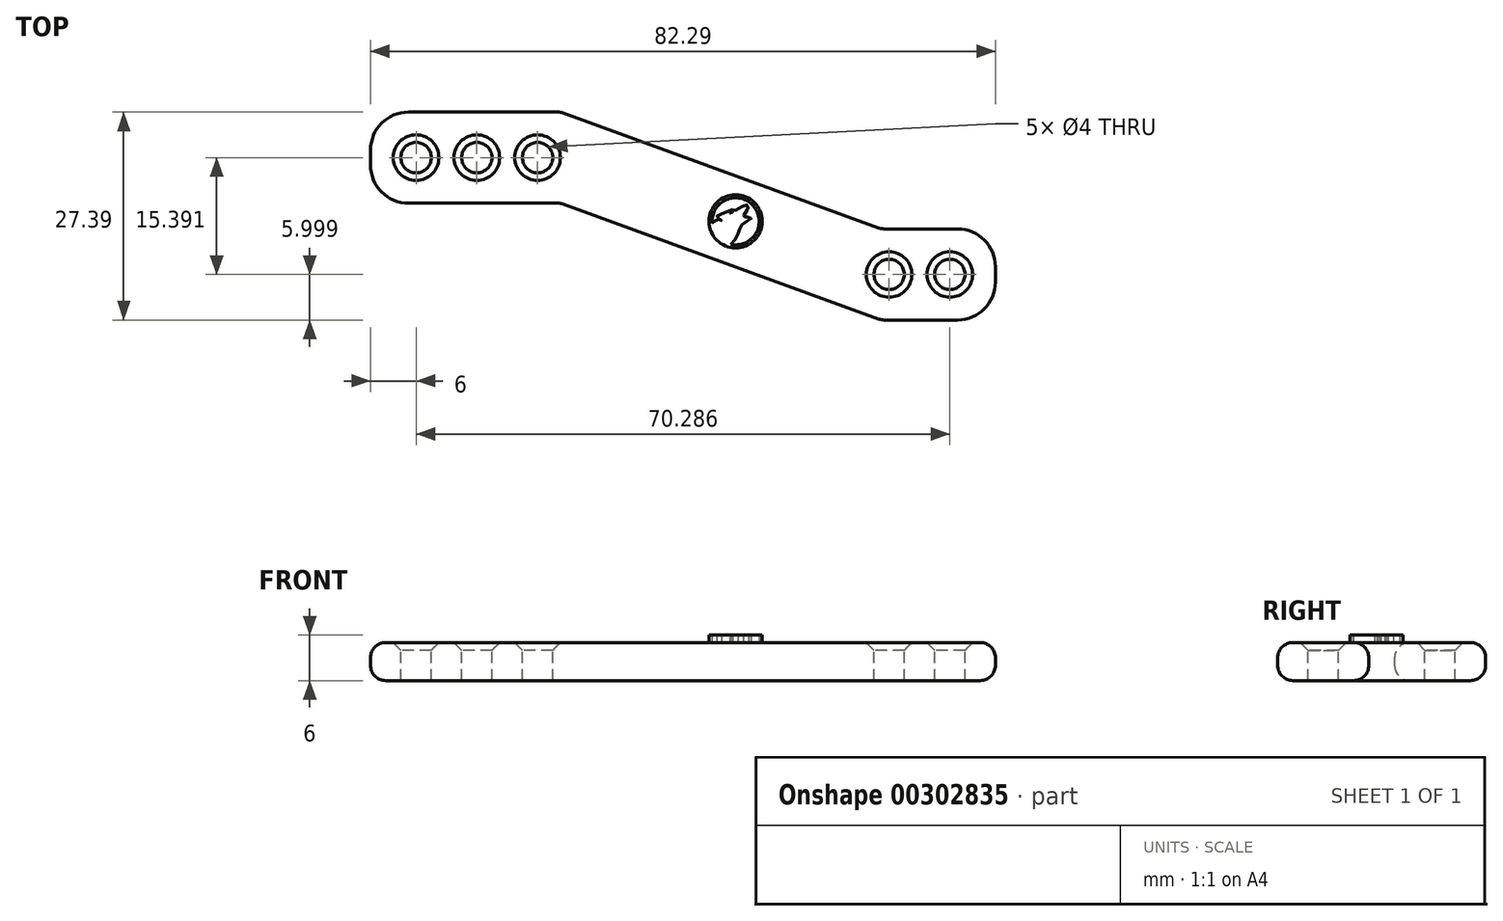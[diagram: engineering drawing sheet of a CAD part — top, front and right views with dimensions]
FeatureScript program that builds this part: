
annotation { "Feature Type Name" : "Feature", "Feature Type Description" : "" }
export const myFeature = defineFeature(function(context is Context, id is Id, definition is map)
    precondition{}
    {
        {
            var Q0;
            Q0=qCreatedBy(makeId("Top.planeOp"),FACE);
            var sketch = newSketch(context, id + "F0", { "sketchPlane" : qUnion([Q0])});
            skLineSegment(sketch, "E0.bottom", {"start": v(0, 0) * mm, "end": v(25, 0) * mm});
            skLineSegment(sketch, "E0.top", {"start": v(0, 12) * mm, "end": v(25, 12) * mm});
            skLineSegment(sketch, "E0.left", {"start": v(0, 0) * mm, "end": v(0, 12) * mm});
            skLineSegment(sketch, "E0.right", {"start": v(25, 0) * mm, "end": v(25, 12) * mm});
            skLineSegment(sketch, "E1", {"start": v(25, 12) * mm, "end": v(67.29, -3.4) * mm});
            skLineSegment(sketch, "E2.bottom", {"start": v(67.29, -3.4) * mm, "end": v(82.29, -3.4) * mm});
            skLineSegment(sketch, "E2.top", {"start": v(67.29, -15.4) * mm, "end": v(82.29, -15.4) * mm});
            skLineSegment(sketch, "E2.left", {"start": v(67.29, -3.4) * mm, "end": v(67.29, -15.4) * mm});
            skLineSegment(sketch, "E2.right", {"start": v(82.29, -3.4) * mm, "end": v(82.29, -15.4) * mm});
            skLineSegment(sketch, "E3", {"start": v(67.29, -15.4) * mm, "end": v(25, 0) * mm});
            skSolve(sketch);
        }
        {
            var Q0;
            Q0=makeQuery(id+"F0.imprint","IMPRINT",FACE,{"disambiguationData":[TD([[makeQuery(id+"F0.imprint","IMPRINT",EDGE,{"derivedFrom":sQuery(id+"F0.wireOp",EDGE,"E0.bottom")}),1.0]])]});
            var Q1;
            Q1=makeQuery(id+"F0.imprint","IMPRINT",FACE,{"disambiguationData":[TD([[makeQuery(id+"F0.imprint","IMPRINT",EDGE,{"derivedFrom":sQuery(id+"F0.wireOp",EDGE,"E2.bottom")}),-1.0]])]});
            var Q2;
            Q2=makeQuery(id+"F0.imprint","IMPRINT",FACE,{"disambiguationData":[TD([[makeQuery(id+"F0.imprint","IMPRINT",EDGE,{"derivedFrom":sQuery(id+"F0.wireOp",EDGE,"E0.right")}),-1.0]])]});
            extrude(context, id + "F1", {"entities" : qUnion([Q0, Q1, Q2]), "depth" : 5 * mm});
        }
        {
            var Q0;
            Q0=makeQuery(id+"F1.opExtrude","CAP_FACE",FACE,{"disambiguationData":[OSD([sQuery(id+"F0.wireOp",EDGE,"E0.bottom"),sQuery(id+"F0.wireOp",EDGE,"E0.top"),sQuery(id+"F0.wireOp",EDGE,"E0.left"),sQuery(id+"F0.wireOp",EDGE,"E1"),sQuery(id+"F0.wireOp",EDGE,"E2.bottom"),sQuery(id+"F0.wireOp",EDGE,"E2.top"),sQuery(id+"F0.wireOp",EDGE,"E2.right"),sQuery(id+"F0.wireOp",EDGE,"E3")])],"isStart":false});
            var sketch = newSketch(context, id + "F2", { "sketchPlane" : qUnion([Q0])});
            skCircle(sketch, "E4", {"center": v(6, 6) * mm, "radius": 2 * mm});
            skPoint(sketch, "E4.centerSnap0", {"position": v(0, 6) * mm});
            skCircle(sketch, "E5", {"center": v(76.29, -9.4) * mm, "radius": 2 * mm});
            skPoint(sketch, "E5.centerSnap0", {"position": v(82.29, -9.4) * mm});
            skCircle(sketch, "E6.1.0.0", {"center": v(14, 6) * mm, "radius": 2 * mm});
            skCircle(sketch, "E6.2.0.0", {"center": v(22, 6) * mm, "radius": 2 * mm});
            skLineSegment(sketch, "E6.direction1", {"start": v(6, 6) * mm, "end": v(14, 6) * mm, "construction": true});
            skCircle(sketch, "E7.1.0.0", {"center": v(68.29, -9.4) * mm, "radius": 2 * mm});
            skLineSegment(sketch, "E7.direction1", {"start": v(76.29, -9.4) * mm, "end": v(68.29, -9.4) * mm, "construction": true});
            skSolve(sketch);
        }
        {
            var Q0;
            Q0=makeQuery(id+"F2.imprint","IMPRINT",FACE,{"disambiguationData":[TD([[makeQuery(id+"F2.imprint","IMPRINT",EDGE,{"derivedFrom":sQuery(id+"F2.wireOp",EDGE,"E4")}),1.0]])]});
            var Q1;
            Q1=makeQuery(id+"F2.imprint","IMPRINT",FACE,{"disambiguationData":[TD([[makeQuery(id+"F2.imprint","IMPRINT",EDGE,{"derivedFrom":sQuery(id+"F2.wireOp",EDGE,"E6.1.0.0")}),1.0]])]});
            var Q2;
            Q2=makeQuery(id+"F2.imprint","IMPRINT",FACE,{"disambiguationData":[TD([[makeQuery(id+"F2.imprint","IMPRINT",EDGE,{"derivedFrom":sQuery(id+"F2.wireOp",EDGE,"E6.2.0.0")}),1.0]])]});
            var Q3;
            Q3=makeQuery(id+"F2.imprint","IMPRINT",FACE,{"disambiguationData":[TD([[makeQuery(id+"F2.imprint","IMPRINT",EDGE,{"derivedFrom":sQuery(id+"F2.wireOp",EDGE,"E7.1.0.0")}),1.0]])]});
            var Q4;
            Q4=makeQuery(id+"F2.imprint","IMPRINT",FACE,{"disambiguationData":[TD([[makeQuery(id+"F2.imprint","IMPRINT",EDGE,{"derivedFrom":sQuery(id+"F2.wireOp",EDGE,"E5")}),1.0]])]});
            extrude(context, id + "F3", {"entities" : qUnion([Q0, Q1, Q2, Q3, Q4]), "operationType" : NewBodyOperationType.REMOVE, "endBound" : BoundingType.THROUGH_ALL, "oppositeDirection" : true, "depth" : 25 * mm});
        }
        {
            var Q0;
            Q0=makeQuery(id+"F1.opExtrude","CAP_EDGE",EDGE,{"disambiguationData":[OSD([sQuery(id+"F0.wireOp",EDGE,"E0.top")])],"isStart":false});
            var Q1;
            Q1=makeQuery(id+"F1.opExtrude","CAP_EDGE",EDGE,{"disambiguationData":[OSD([sQuery(id+"F0.wireOp",EDGE,"E0.top")])],"isStart":true});
            var Q2;
            Q2=makeQuery(id+"F1.opExtrude","CAP_EDGE",EDGE,{"disambiguationData":[OSD([sQuery(id+"F0.wireOp",EDGE,"E0.left")])],"isStart":false});
            var Q3;
            Q3=makeQuery(id+"F1.opExtrude","CAP_EDGE",EDGE,{"disambiguationData":[OSD([sQuery(id+"F0.wireOp",EDGE,"E0.left")])],"isStart":true});
            var Q4;
            Q4=makeQuery(id+"F1.opExtrude","CAP_EDGE",EDGE,{"disambiguationData":[OSD([sQuery(id+"F0.wireOp",EDGE,"E0.bottom")])],"isStart":false});
            var Q5;
            Q5=makeQuery(id+"F1.opExtrude","CAP_EDGE",EDGE,{"disambiguationData":[OSD([sQuery(id+"F0.wireOp",EDGE,"E0.bottom")])],"isStart":true});
            var Q6;
            Q6=makeQuery(id+"F1.opExtrude","CAP_EDGE",EDGE,{"disambiguationData":[OSD([sQuery(id+"F0.wireOp",EDGE,"E3")])],"isStart":false});
            var Q7;
            Q7=makeQuery(id+"F1.opExtrude","CAP_EDGE",EDGE,{"disambiguationData":[OSD([sQuery(id+"F0.wireOp",EDGE,"E2.top")])],"isStart":false});
            var Q8;
            Q8=makeQuery(id+"F1.opExtrude","CAP_EDGE",EDGE,{"disambiguationData":[OSD([sQuery(id+"F0.wireOp",EDGE,"E3")])],"isStart":true});
            var Q9;
            Q9=makeQuery(id+"F1.opExtrude","CAP_EDGE",EDGE,{"disambiguationData":[OSD([sQuery(id+"F0.wireOp",EDGE,"E2.top")])],"isStart":true});
            var Q10;
            Q10=makeQuery(id+"F1.opExtrude","CAP_EDGE",EDGE,{"disambiguationData":[OSD([sQuery(id+"F0.wireOp",EDGE,"E2.right")])],"isStart":false});
            var Q11;
            Q11=makeQuery(id+"F1.opExtrude","CAP_EDGE",EDGE,{"disambiguationData":[OSD([sQuery(id+"F0.wireOp",EDGE,"E2.right")])],"isStart":true});
            var Q12;
            Q12=makeQuery(id+"F1.opExtrude","CAP_EDGE",EDGE,{"disambiguationData":[OSD([sQuery(id+"F0.wireOp",EDGE,"E2.bottom")])],"isStart":true});
            var Q13;
            Q13=makeQuery(id+"F1.opExtrude","CAP_EDGE",EDGE,{"disambiguationData":[OSD([sQuery(id+"F0.wireOp",EDGE,"E2.bottom")])],"isStart":false});
            var Q14;
            Q14=makeQuery(id+"F1.opExtrude","CAP_EDGE",EDGE,{"disambiguationData":[OSD([sQuery(id+"F0.wireOp",EDGE,"E1")])],"isStart":false});
            var Q15;
            Q15=makeQuery(id+"F1.opExtrude","CAP_EDGE",EDGE,{"disambiguationData":[OSD([sQuery(id+"F0.wireOp",EDGE,"E1")])],"isStart":true});
            var Q16;
            Q16=makeQuery(id+"F1.opExtrude","SWEPT_EDGE",EDGE,{"disambiguationData":[OSD([sQuery(id+"F0.wireOp",EDGE,"E0.top"),sQuery(id+"F0.wireOp",EDGE,"E0.right"),sQuery(id+"F0.wireOp",EDGE,"E1")])]});
            var Q17;
            Q17=makeQuery(id+"F1.opExtrude","SWEPT_EDGE",EDGE,{"disambiguationData":[OSD([sQuery(id+"F0.wireOp",EDGE,"E1"),sQuery(id+"F0.wireOp",EDGE,"E2.bottom"),sQuery(id+"F0.wireOp",EDGE,"E2.left")])]});
            var Q18;
            Q18=makeQuery(id+"F1.opExtrude","SWEPT_EDGE",EDGE,{"disambiguationData":[OSD([sQuery(id+"F0.wireOp",EDGE,"E2.top"),sQuery(id+"F0.wireOp",EDGE,"E2.left"),sQuery(id+"F0.wireOp",EDGE,"E3")])]});
            var Q19;
            Q19=makeQuery(id+"F1.opExtrude","SWEPT_EDGE",EDGE,{"disambiguationData":[OSD([sQuery(id+"F0.wireOp",EDGE,"E0.bottom"),sQuery(id+"F0.wireOp",EDGE,"E0.right"),sQuery(id+"F0.wireOp",EDGE,"E3")])]});
            fillet(context, id + "F4", {"entities" : qUnion([Q0, Q1, Q2, Q3, Q4, Q5, Q6, Q7, Q8, Q9, Q10, Q11, Q12, Q13, Q14, Q15, Q16, Q17, Q18, Q19]), "radius" : 2 * mm, "tangentPropagation" : true, "allowEdgeOverflow" : false});
        }
        {
            var Q0;
            Q0=makeQuery(id+"F1.opExtrude","SWEPT_EDGE",EDGE,{"disambiguationData":[OSD([sQuery(id+"F0.wireOp",EDGE,"E0.bottom"),sQuery(id+"F0.wireOp",EDGE,"E0.left")])]});
            var Q1;
            Q1=makeQuery(id+"F4.opFillet","BLEND_EDGE",EDGE,{"blendedFrom":[makeQuery(id+"F1.opExtrude","CAP_EDGE",EDGE,{"disambiguationData":[OSD([sQuery(id+"F0.wireOp",EDGE,"E0.bottom")])],"isStart":false}),makeQuery(id+"F1.opExtrude","CAP_EDGE",EDGE,{"disambiguationData":[OSD([sQuery(id+"F0.wireOp",EDGE,"E0.left")])],"isStart":false})],"blendedInto":[]});
            var Q2;
            Q2=makeQuery(id+"F4.opFillet","BLEND_EDGE",EDGE,{"blendedFrom":[makeQuery(id+"F1.opExtrude","CAP_EDGE",EDGE,{"disambiguationData":[OSD([sQuery(id+"F0.wireOp",EDGE,"E0.bottom")])],"isStart":true}),makeQuery(id+"F1.opExtrude","CAP_EDGE",EDGE,{"disambiguationData":[OSD([sQuery(id+"F0.wireOp",EDGE,"E0.left")])],"isStart":true})],"blendedInto":[]});
            var Q3;
            Q3=makeQuery(id+"F4.opFillet","BLEND_EDGE",EDGE,{"blendedFrom":[makeQuery(id+"F1.opExtrude","CAP_EDGE",EDGE,{"disambiguationData":[OSD([sQuery(id+"F0.wireOp",EDGE,"E0.top")])],"isStart":false}),makeQuery(id+"F1.opExtrude","CAP_EDGE",EDGE,{"disambiguationData":[OSD([sQuery(id+"F0.wireOp",EDGE,"E0.left")])],"isStart":false})],"blendedInto":[]});
            var Q4;
            Q4=makeQuery(id+"F4.opFillet","BLEND_EDGE",EDGE,{"blendedFrom":[makeQuery(id+"F1.opExtrude","CAP_EDGE",EDGE,{"disambiguationData":[OSD([sQuery(id+"F0.wireOp",EDGE,"E2.bottom")])],"isStart":false}),makeQuery(id+"F1.opExtrude","CAP_EDGE",EDGE,{"disambiguationData":[OSD([sQuery(id+"F0.wireOp",EDGE,"E2.right")])],"isStart":false})],"blendedInto":[]});
            var Q5;
            Q5=makeQuery(id+"F4.opFillet","BLEND_EDGE",EDGE,{"blendedFrom":[makeQuery(id+"F1.opExtrude","CAP_EDGE",EDGE,{"disambiguationData":[OSD([sQuery(id+"F0.wireOp",EDGE,"E2.top")])],"isStart":false}),makeQuery(id+"F1.opExtrude","CAP_EDGE",EDGE,{"disambiguationData":[OSD([sQuery(id+"F0.wireOp",EDGE,"E2.right")])],"isStart":false})],"blendedInto":[]});
            fillet(context, id + "F5", {"entities" : qUnion([Q0, Q1, Q2, Q3, Q4, Q5]), "radius" : 5 * mm, "tangentPropagation" : true, "allowEdgeOverflow" : false});
        }
        {
            var Q0;
            Q0=makeQuery(id+"F1.opExtrude","CAP_FACE",FACE,{"disambiguationData":[OSD([sQuery(id+"F0.wireOp",EDGE,"E0.bottom"),sQuery(id+"F0.wireOp",EDGE,"E0.top"),sQuery(id+"F0.wireOp",EDGE,"E0.left"),sQuery(id+"F0.wireOp",EDGE,"E1"),sQuery(id+"F0.wireOp",EDGE,"E2.bottom"),sQuery(id+"F0.wireOp",EDGE,"E2.top"),sQuery(id+"F0.wireOp",EDGE,"E2.right"),sQuery(id+"F0.wireOp",EDGE,"E3")])],"isStart":false});
            chamfer(context, id + "F6", {"entities" : qUnion([Q0]), "width" : 1 * mm, "tangentPropagation" : true});
        }
        {
            var Q0;
            Q0=makeQuery(id+"F1.opExtrude","CAP_FACE",FACE,{"disambiguationData":[OSD([sQuery(id+"F0.wireOp",EDGE,"E0.bottom"),sQuery(id+"F0.wireOp",EDGE,"E0.top"),sQuery(id+"F0.wireOp",EDGE,"E0.left"),sQuery(id+"F0.wireOp",EDGE,"E1"),sQuery(id+"F0.wireOp",EDGE,"E2.bottom"),sQuery(id+"F0.wireOp",EDGE,"E2.top"),sQuery(id+"F0.wireOp",EDGE,"E2.right"),sQuery(id+"F0.wireOp",EDGE,"E3")])],"isStart":false});
            var sketch = newSketch(context, id + "F7", { "sketchPlane" : qUnion([Q0])});
            skLineSegment(sketch, "E8", {"start": v(46.83, -5.82) * mm, "end": v(48.07, -2.4) * mm});
            skCircle(sketch, "E9", {"center": v(48.07, -2.4) * mm, "radius": 3.5 * mm});
            skCircle(sketch, "E10.0", {"center": v(48.07, -2.4) * mm, "radius": 3.1 * mm});
            skFitSpline(sketch, "E11", {"points": [v(47.43, -5.43) * mm, v(48.01, -4.83) * mm, v(48.38, -4.04) * mm, v(48.4, -3.62) * mm, v(48.78, -3.22) * mm, v(49.01, -2.61) * mm, v(49.83, -2.3) * mm, v(50.12, -2.06) * mm, v(49.94, -1.88) * mm, v(49.6, -1.86) * mm, v(49.48, -1.9) * mm, v(49.38, -1.84) * mm, v(49.3, -1.88) * mm, v(49.08, -1.88) * mm, v(49.58, -0.86) * mm, v(49.6, -0.89) * mm, v(49.66, -0.84) * mm, v(49.68, -0.74) * mm, v(49.75, -0.62) * mm, v(49.68, -0.41) * mm, v(49.52, -0.18) * mm, v(49.37, -0.19) * mm, v(48.1, -0.93) * mm, v(48, -0.9) * mm, v(47.67, -0.85) * mm, v(47.38, -0.92) * mm, v(47.12, -1.1) * mm, v(47.07, -1.16) * mm, v(45.6, -1.63) * mm, v(45.61, -1.66) * mm, v(45.68, -1.8) * mm, v(45.76, -2) * mm, v(45.94, -2.1) * mm, v(46.23, -2.29) * mm, v(45.95, -2.26) * mm, v(45.82, -2.16) * mm, v(45.62, -2.13) * mm, v(45.35, -2.35) * mm, v(45.1, -2.55) * mm, v(44.98, -2.64) * mm], "startDerivative": vector(14.17, 12.65) * mm, "endDerivative": vector(-6.5, -4.2) * mm});
            skFitSpline(sketch, "E12", {"points": [v(47.32, -1.3) * mm, v(47.33, -1.28) * mm, v(47.44, -1.2) * mm, v(47.62, -1.13) * mm, v(47.71, -1.15) * mm, v(47.63, -1.19) * mm, v(47.54, -1.22) * mm, v(47.43, -1.27) * mm, v(47.32, -1.3) * mm]});
            skSolve(sketch);
        }
        {
            var Q0;
            Q0=makeQuery(id+"F7.imprint","IMPRINT",FACE,{"disambiguationData":[TD([[makeQuery(id+"F7.imprint","IMPRINT",EDGE,{"derivedFrom":sQuery(id+"F7.wireOp",EDGE,"E9")}),1.0]])]});
            var Q1;
            {var subQ0=sQuery(id+"F7.wireOp",EDGE,"E11");Q1=makeQuery(id+"F7.imprint","IMPRINT",FACE,{"disambiguationData":[TD([[makeQuery(id+"F7.imprint","IMPRINT",EDGE,{"derivedFrom":subQ0}),1.0]])]});}
            extrude(context, id + "F8", {"entities" : qUnion([Q0, Q1]), "operationType" : NewBodyOperationType.ADD, "depth" : 1 * mm});
        }
    });
